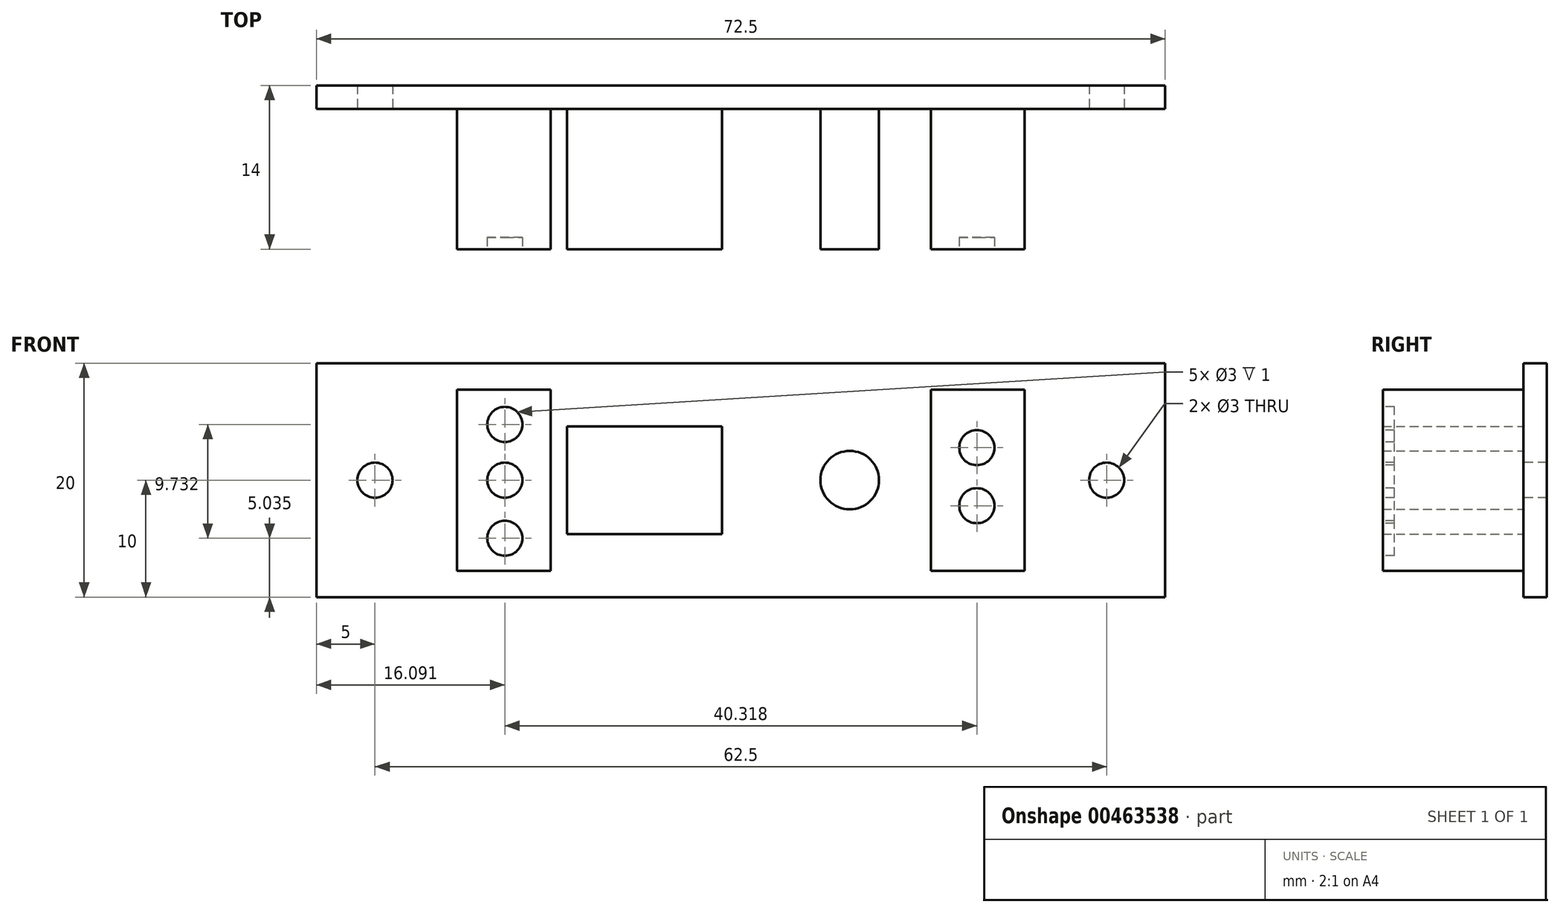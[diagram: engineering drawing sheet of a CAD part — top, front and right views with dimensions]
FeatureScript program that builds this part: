
annotation { "Feature Type Name" : "Feature", "Feature Type Description" : "" }
export const myFeature = defineFeature(function(context is Context, id is Id, definition is map)
    precondition{}
    {
        {
            var Q0;
            Q0=qCreatedBy(makeId("Front.planeOp"),FACE);
            var sketch = newSketch(context, id + "F0", { "sketchPlane" : qUnion([Q0])});
            skLineSegment(sketch, "E0.bottom", {"start": v(36.25, 10) * mm, "end": v(-36.25, 10) * mm});
            skLineSegment(sketch, "E0.top", {"start": v(36.25, -10) * mm, "end": v(-36.25, -10) * mm});
            skLineSegment(sketch, "E0.left", {"start": v(36.25, 10) * mm, "end": v(36.25, -10) * mm});
            skLineSegment(sketch, "E0.right", {"start": v(-36.25, 10) * mm, "end": v(-36.25, -10) * mm});
            skPoint(sketch, "E0.middle", {"position": v(0, 0) * mm});
            skSolve(sketch);
        }
        {
            var Q0;
            Q0=makeQuery(id+"F0.imprint","IMPRINT",FACE,{"disambiguationData":[TD([[makeQuery(id+"F0.imprint","IMPRINT",EDGE,{"derivedFrom":sQuery(id+"F0.wireOp",EDGE,"E0.bottom")}),1.0]])]});
            extrude(context, id + "F1", {"entities" : qUnion([Q0]), "oppositeDirection" : true, "depth" : 2 * mm, "offsetDistance" : 25 * mm});
        }
        {
            var Q0;
            Q0=makeQuery(id+"F1.opExtrude","CAP_FACE",FACE,{"disambiguationData":[OSD([sQuery(id+"F0.wireOp",EDGE,"E0.bottom"),sQuery(id+"F0.wireOp",EDGE,"E0.top"),sQuery(id+"F0.wireOp",EDGE,"E0.left"),sQuery(id+"F0.wireOp",EDGE,"E0.right")])],"isStart":true});
            var sketch = newSketch(context, id + "F2", { "sketchPlane" : qUnion([Q0])});
            skCircle(sketch, "E1", {"center": v(-31.25, 0) * mm, "radius": 1.5 * mm});
            skCircle(sketch, "E2", {"center": v(31.25, 0) * mm, "radius": 1.5 * mm});
            skSolve(sketch);
        }
        {
            var Q0;
            Q0 = qSketchRegion(id + "F2", true);
            extrude(context, id + "F3", {"entities" : qUnion([Q0]), "operationType" : NewBodyOperationType.REMOVE, "endBound" : BoundingType.UP_TO_NEXT, "oppositeDirection" : true, "depth" : 25 * mm, "offsetDistance" : 25 * mm});
        }
        {
            var Q0;
            Q0=makeQuery(id+"F1.opExtrude","CAP_FACE",FACE,{"disambiguationData":[OSD([sQuery(id+"F0.wireOp",EDGE,"E0.bottom"),sQuery(id+"F0.wireOp",EDGE,"E0.top"),sQuery(id+"F0.wireOp",EDGE,"E0.left"),sQuery(id+"F0.wireOp",EDGE,"E0.right")])],"isStart":true});
            var sketch = newSketch(context, id + "F4", { "sketchPlane" : qUnion([Q0])});
            skLineSegment(sketch, "E3.bottom", {"start": v(-16.25, 7.75) * mm, "end": v(-24.25, 7.75) * mm});
            skLineSegment(sketch, "E3.top", {"start": v(-16.25, -7.75) * mm, "end": v(-24.25, -7.75) * mm});
            skLineSegment(sketch, "E3.left", {"start": v(-16.25, 7.75) * mm, "end": v(-16.25, -7.75) * mm});
            skLineSegment(sketch, "E3.right", {"start": v(-24.25, 7.75) * mm, "end": v(-24.25, -7.75) * mm});
            skPoint(sketch, "E3.middle", {"position": v(-20.25, 0) * mm});
            skLineSegment(sketch, "E4.bottom", {"start": v(24.25, 7.75) * mm, "end": v(16.25, 7.75) * mm});
            skLineSegment(sketch, "E4.top", {"start": v(24.25, -7.75) * mm, "end": v(16.25, -7.75) * mm});
            skLineSegment(sketch, "E4.left", {"start": v(24.25, 7.75) * mm, "end": v(24.25, -7.75) * mm});
            skLineSegment(sketch, "E4.right", {"start": v(16.25, 7.75) * mm, "end": v(16.25, -7.75) * mm});
            skPoint(sketch, "E4.middle", {"position": v(20.25, 0) * mm});
            skLineSegment(sketch, "E5.bottom", {"start": v(-1.62, 4.6) * mm, "end": v(-14.83, 4.6) * mm});
            skLineSegment(sketch, "E5.top", {"start": v(-1.62, -4.6) * mm, "end": v(-14.83, -4.6) * mm});
            skLineSegment(sketch, "E5.left", {"start": v(-1.62, 4.6) * mm, "end": v(-1.62, -4.6) * mm});
            skLineSegment(sketch, "E5.right", {"start": v(-14.83, 4.6) * mm, "end": v(-14.83, -4.6) * mm});
            skPoint(sketch, "E5.middle", {"position": v(-8.22, 0) * mm});
            skCircle(sketch, "E6", {"center": v(9.3, 0) * mm, "radius": 2.5 * mm});
            skSolve(sketch);
        }
        {
            var Q0;
            Q0 = qSketchRegion(id + "F4", true);
            extrude(context, id + "F5", {"entities" : qUnion([Q0]), "operationType" : NewBodyOperationType.ADD, "depth" : 12 * mm, "offsetDistance" : 25 * mm});
        }
        {
            var Q0;
            Q0=makeQuery(id+"F5.opExtrude","CAP_FACE",FACE,{"disambiguationData":[OSD([sQuery(id+"F4.wireOp",EDGE,"E3.bottom"),sQuery(id+"F4.wireOp",EDGE,"E3.top"),sQuery(id+"F4.wireOp",EDGE,"E3.left"),sQuery(id+"F4.wireOp",EDGE,"E3.right")])],"isStart":false});
            var sketch = newSketch(context, id + "F6", { "sketchPlane" : qUnion([Q0])});
            skCircle(sketch, "E7", {"center": v(-20.16, 4.77) * mm, "radius": 1.5 * mm});
            skCircle(sketch, "E8", {"center": v(-20.16, 0) * mm, "radius": 1.5 * mm});
            skCircle(sketch, "E9", {"center": v(-20.16, -4.97) * mm, "radius": 1.5 * mm});
            skCircle(sketch, "E10", {"center": v(20.16, 2.78) * mm, "radius": 1.5 * mm});
            skCircle(sketch, "E11", {"center": v(20.16, -2.18) * mm, "radius": 1.5 * mm});
            skSolve(sketch);
        }
        {
            var Q0;
            Q0 = qSketchRegion(id + "F6", true);
            extrude(context, id + "F7", {"entities" : qUnion([Q0]), "operationType" : NewBodyOperationType.REMOVE, "oppositeDirection" : true, "depth" : 1 * mm, "offsetDistance" : 25 * mm});
        }
    });
